# Revit family: dice_on_320-0650
name_source: partatom
category: Lighting Fixtures
units: mm (PartAtom-declared; Revit-internal decimal feet)

## family parameters
Cut with Voids When Loaded = No
Host = Face
Light Source = No
Part Type = Normal
Room Calculation Point = No
Round Connector Dimension = Use Diameter
Shared = No

## types (1)
- 320-0650-K14 (1 x LED, 1012.18 lm, 10.1 W, 2700K)
    Apparent Load = 10 VA
    CIE Flux Codes = 99 100 100 100 65
    Color Rendering = 1A/90…99
    Color Temperature = 2700K
    Default Elevation = 1800 mm
    Description = DICE ON
    Height = 125 mm
    Lamp = 1 x LED
    Lamp Light Flux = 1012.18 lm
    Lamp Power = 10.1 W
    Lamp count = 1
    Length = 74 mm
    Luminous efficacy = 65 lm/W
    Manufacturer = Prolicht
    ModVariant = No
    Model = 320-0650
    Mounting Place = Ceiling
    Mounting Type = Surface mounted
    Number of Poles = 1
    OnlyDefault = Yes
    Power Factor = 1
    Product Name = DICE ON
    Product group = Surface spotlights
    ProductGroupID = 332
    Protection Class = Protection class
    Protection Degree = Degree of protection
    RLX_Detail_Level = 1
    RlxData = <blob elided: 113269 chars, md5=2b32eff5>
    Socket = socket
    Standby Power = 0 W
    System Light Flux = 657 lm
    System Power = 10 W
    Type Comments = REFLECTOR 14° (14)
    Type Image = 320-0650.jpg
    URL = http://relux.com
    VarID = 320-0650-k14
    Voltage = 0 V
    Weight = 0.00 kg
    Width = 0 mm  [stored 0 ft]

note: [stored X ft] marks values corroborated as IEEE doubles in the binary element streams (Revit-internal decimal feet)

## geometry (parser evidence)
native form markers: Sweep x9
no freeform markers — native parametric forms only
